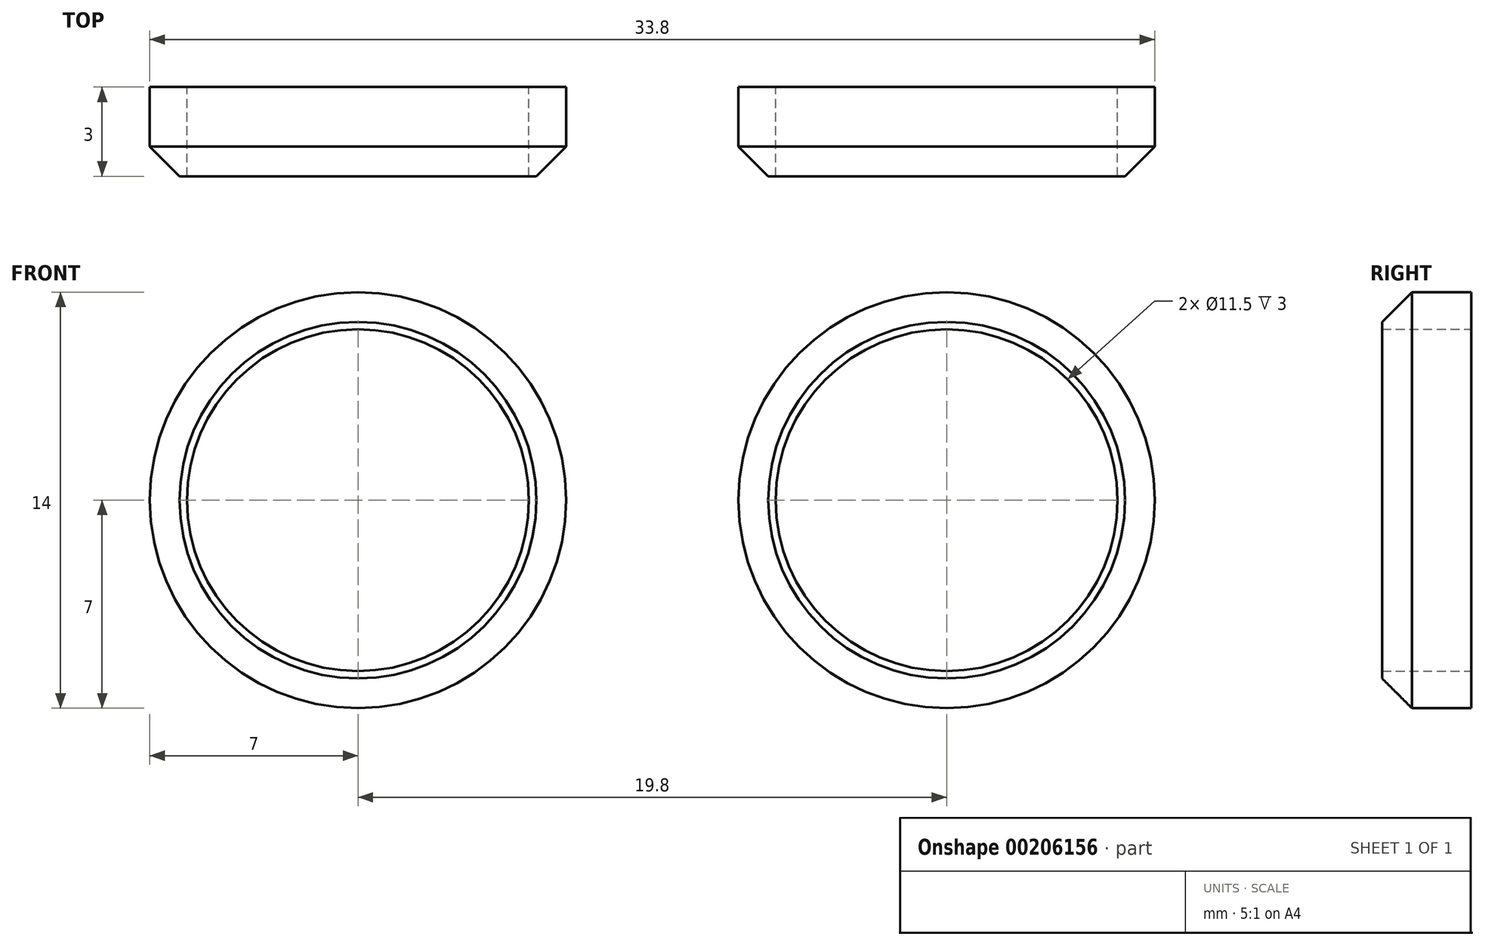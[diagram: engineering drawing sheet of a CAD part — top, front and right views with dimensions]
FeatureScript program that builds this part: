
annotation { "Feature Type Name" : "Feature", "Feature Type Description" : "" }
export const myFeature = defineFeature(function(context is Context, id is Id, definition is map)
    precondition{}
    {
        {
            var Q0;
            Q0=qCreatedBy(makeId("Front.planeOp"),FACE);
            var sketch = newSketch(context, id + "F0", { "sketchPlane" : qUnion([Q0])});
            skCircle(sketch, "E0", {"center": v(0, 0) * mm, "radius": 5.75 * mm});
            skCircle(sketch, "E1", {"center": v(0, 0) * mm, "radius": 7 * mm});
            skSolve(sketch);
        }
        {
            var Q0;
            Q0 = qSketchRegion(id + "F0", true);
            extrude(context, id + "F1", {"entities" : qUnion([Q0]), "depth" : 3 * mm});
        }
        {
            var Q0;
            Q0=makeQuery(id+"F1.opExtrude","CAP_EDGE",EDGE,{"disambiguationData":[OSD([sQuery(id+"F0.wireOp",EDGE,"E1")])],"isStart":false});
            chamfer(context, id + "F2", {"entities" : qUnion([Q0]), "width" : 1 * mm, "tangentPropagation" : true});
        }
        {
            var Q0;
            Q0=makeQuery(id+"F1.opExtrude","SWEPT_BODY",BODY,{"disambiguationData":[OSD([sQuery(id+"F0.wireOp",EDGE,"E0"),sQuery(id+"F0.wireOp",EDGE,"E1")])]});
            transform(context, id + "F3", {"entities" : qUnion([Q0]), "transformType" : TransformType.TRANSLATION_3D, "dx" : 19.8 * mm, "dy" : 0 * mm, "dz" : 0 * mm, "makeCopy" : true});
        }
    });
